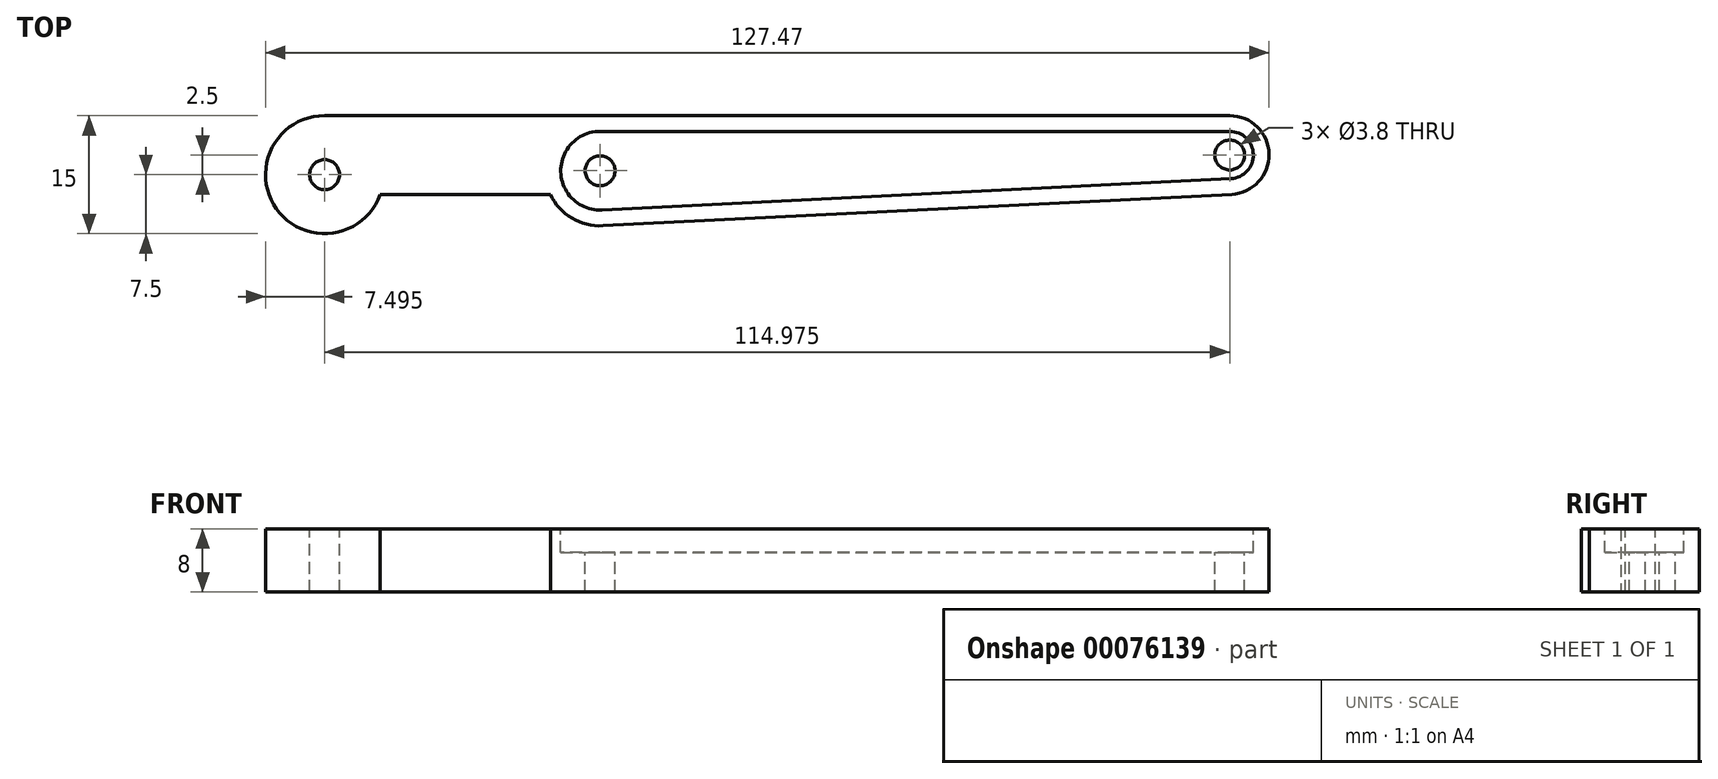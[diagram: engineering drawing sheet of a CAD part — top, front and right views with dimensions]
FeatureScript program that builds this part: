
annotation { "Feature Type Name" : "Feature", "Feature Type Description" : "" }
export const myFeature = defineFeature(function(context is Context, id is Id, definition is map)
    precondition{}
    {
        {
            var Q0;
            Q0=qCreatedBy(makeId("Top.planeOp"),FACE);
            var sketch = newSketch(context, id + "F0", { "sketchPlane" : qUnion([Q0])});
            skCircle(sketch, "E0", {"center": v(0, 0) * mm, "radius": 5 * mm});
            skCircle(sketch, "E1", {"center": v(-2, 79.97) * mm, "radius": 7 * mm});
            skLineSegment(sketch, "E2", {"start": v(-2, 79.97) * mm, "end": v(0, 0) * mm});
            skLineSegment(sketch, "E3", {"start": v(5, 79.97) * mm, "end": v(5, 0) * mm});
            skLineSegment(sketch, "E4", {"start": v(-9, 79.63) * mm, "end": v(-5, -0.25) * mm});
            skLineSegment(sketch, "E5.bottom", {"start": v(5, 79.97) * mm, "end": v(-5, 79.97) * mm});
            skLineSegment(sketch, "E5.top", {"start": v(5, 114.97) * mm, "end": v(-5, 114.97) * mm});
            skLineSegment(sketch, "E5.left", {"start": v(5, 79.97) * mm, "end": v(5, 114.97) * mm});
            skLineSegment(sketch, "E5.right", {"start": v(-5, 79.97) * mm, "end": v(-5, 114.97) * mm});
            skCircle(sketch, "E6", {"center": v(-2.5, 114.97) * mm, "radius": 7.5 * mm});
            skSolve(sketch);
        }
        {
            var Q0;
            Q0 = qSketchRegion(id + "F0", true);
            extrude(context, id + "F1", {"entities" : qUnion([Q0]), "depth" : 8 * mm});
        }
        {
            var Q0;
            Q0=makeQuery(id+"F1.opExtrude","CAP_FACE",FACE,{"disambiguationData":[OSD([sQuery(id+"F0.wireOp",EDGE,"E0"),sQuery(id+"F0.wireOp",EDGE,"E1"),sQuery(id+"F0.wireOp",EDGE,"E3"),sQuery(id+"F0.wireOp",EDGE,"E4"),sQuery(id+"F0.wireOp",EDGE,"E5.left"),sQuery(id+"F0.wireOp",EDGE,"E5.right"),sQuery(id+"F0.wireOp",EDGE,"E6")])],"isStart":false});
            var sketch = newSketch(context, id + "F2", { "sketchPlane" : qUnion([Q0])});
            skCircle(sketch, "E7", {"center": v(0, 0) * mm, "radius": 1.9 * mm});
            skCircle(sketch, "E8", {"center": v(-2, 79.97) * mm, "radius": 1.9 * mm});
            skCircle(sketch, "E9", {"center": v(-2.5, 114.97) * mm, "radius": 1.9 * mm});
            skSolve(sketch);
        }
        {
            var Q0;
            Q0=makeQuery(id+"F2.imprint","IMPRINT",FACE,{"disambiguationData":[TD([[makeQuery(id+"F2.imprint","IMPRINT",EDGE,{"derivedFrom":sQuery(id+"F2.wireOp",EDGE,"E8")}),1.0]])]});
            var Q1;
            Q1=makeQuery(id+"F2.imprint","IMPRINT",FACE,{"disambiguationData":[TD([[makeQuery(id+"F2.imprint","IMPRINT",EDGE,{"derivedFrom":sQuery(id+"F2.wireOp",EDGE,"E9")}),1.0]])]});
            var Q2;
            Q2=makeQuery(id+"F2.imprint","IMPRINT",FACE,{"disambiguationData":[TD([[makeQuery(id+"F2.imprint","IMPRINT",EDGE,{"derivedFrom":sQuery(id+"F2.wireOp",EDGE,"E7")}),1.0]])]});
            extrude(context, id + "F3", {"entities" : qUnion([Q0, Q1, Q2]), "operationType" : NewBodyOperationType.REMOVE, "endBound" : BoundingType.THROUGH_ALL, "oppositeDirection" : true, "depth" : 25 * mm});
        }
        {
            var Q0;
            Q0=makeQuery(id+"F1.opExtrude","CAP_FACE",FACE,{"disambiguationData":[OSD([sQuery(id+"F0.wireOp",EDGE,"E0"),sQuery(id+"F0.wireOp",EDGE,"E1"),sQuery(id+"F0.wireOp",EDGE,"E3"),sQuery(id+"F0.wireOp",EDGE,"E4"),sQuery(id+"F0.wireOp",EDGE,"E5.left"),sQuery(id+"F0.wireOp",EDGE,"E5.right"),sQuery(id+"F0.wireOp",EDGE,"E6")])],"isStart":false});
            var sketch = newSketch(context, id + "F4", { "sketchPlane" : qUnion([Q0])});
            skLineSegment(sketch, "E10.0", {"start": v(3, 0) * mm, "end": v(3, 79.97) * mm});
            skArc(sketch, "E10.1", {"start": v(-3, -0.15) * mm, "mid": v(0.08, -3) * mm, "end": v(3, 0) * mm});
            skLineSegment(sketch, "E10.2", {"start": v(-7, 79.73) * mm, "end": v(-3, -0.15) * mm});
            skArc(sketch, "E10.3", {"start": v(-4.14, 84.5) * mm, "mid": v(-6.3, 82.54) * mm, "end": v(-7, 79.73) * mm});
            skArc(sketch, "E11", {"start": v(3, 79.97) * mm, "mid": v(-2.13, 84.97) * mm, "end": v(-7, 79.73) * mm});
            skSolve(sketch);
        }
        {
            var Q0;
            Q0 = qSketchRegion(id + "F4", true);
            extrude(context, id + "F5", {"entities" : qUnion([Q0]), "operationType" : NewBodyOperationType.REMOVE, "oppositeDirection" : true, "depth" : 3 * mm});
        }
        {
            var Q0;
            Q0=makeQuery(id+"F1.opExtrude","SWEPT_BODY",BODY,{"disambiguationData":[OSD([sQuery(id+"F0.wireOp",EDGE,"E0"),sQuery(id+"F0.wireOp",EDGE,"E1"),sQuery(id+"F0.wireOp",EDGE,"E3"),sQuery(id+"F0.wireOp",EDGE,"E4"),sQuery(id+"F0.wireOp",EDGE,"E5.left"),sQuery(id+"F0.wireOp",EDGE,"E5.right"),sQuery(id+"F0.wireOp",EDGE,"E6")])]});
            var Q1;
            Q1=makeQuery(id+"F5.boolean.opBoolean","INTERSECT",EDGE,{"derivedFrom":[makeQuery(id+"F3.boolean.opBoolean","COPY",FACE,{"derivedFrom":makeQuery(id+"F3.opExtrude","SWEPT_FACE",FACE,{"disambiguationData":[OSD([sQuery(id+"F2.wireOp",EDGE,"E7")])]})}),makeQuery(id+"F5.opExtrude","CAP_FACE",FACE,{"disambiguationData":[OSD([sQuery(id+"F4.wireOp",EDGE,"E10.0"),sQuery(id+"F4.wireOp",EDGE,"E10.1"),sQuery(id+"F4.wireOp",EDGE,"E10.2"),sQuery(id+"F4.wireOp",EDGE,"E11")])],"isStart":false})]});
            transform(context, id + "F6", {"entities" : qUnion([Q0]), "transformType" : TransformType.ROTATION, "transformAxis" : qUnion([Q1]), "angle" : 90 * degree, "makeCopy" : false});
        }
    });
